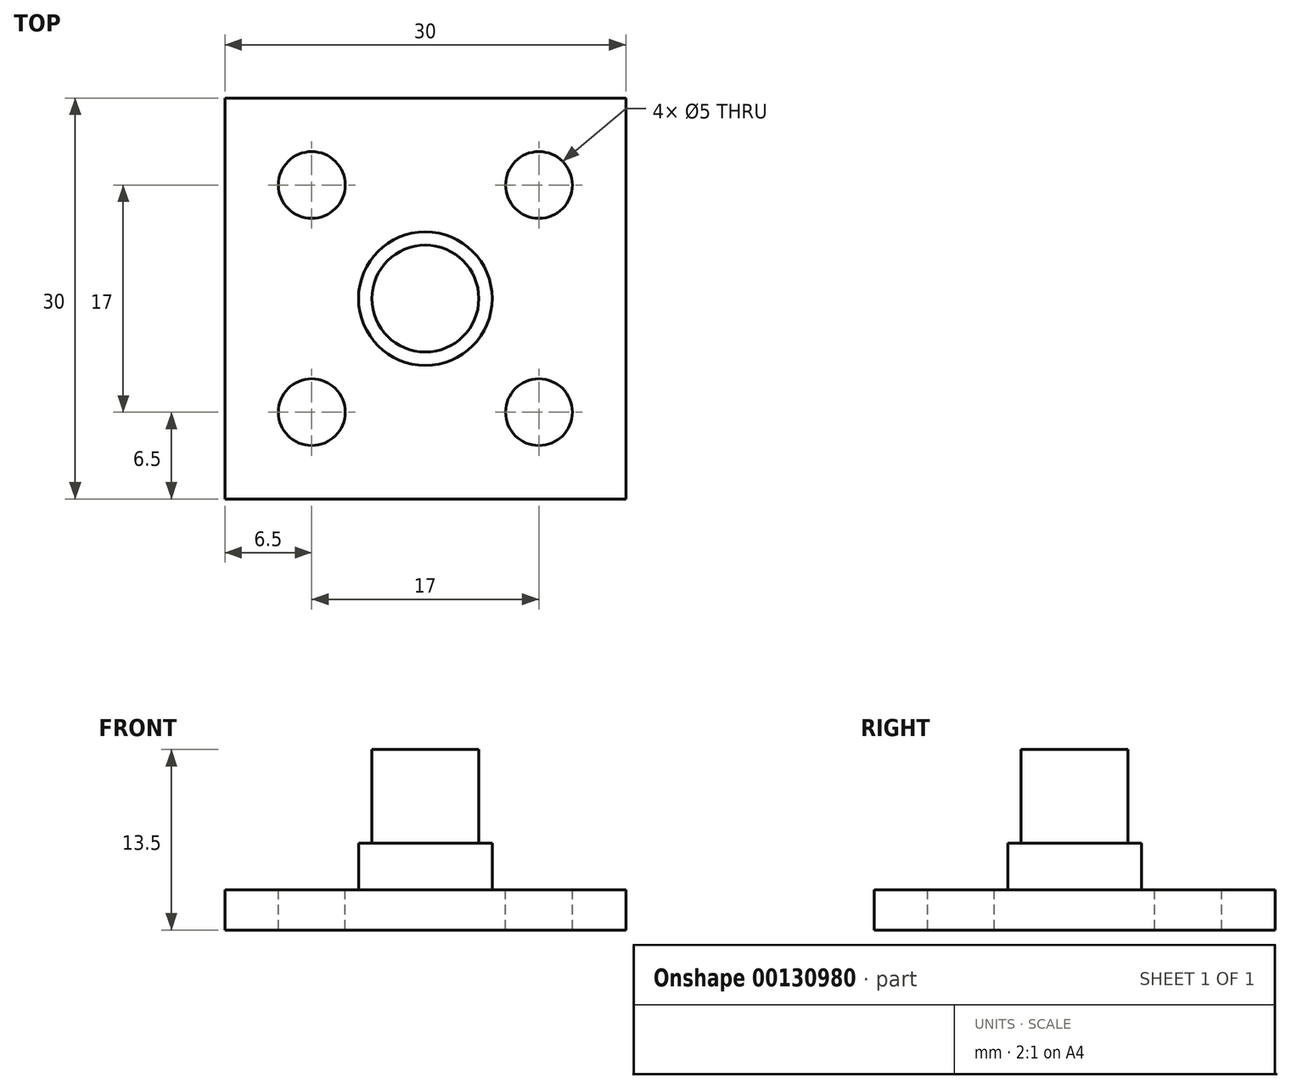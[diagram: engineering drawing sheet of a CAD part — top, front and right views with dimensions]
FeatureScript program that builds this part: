
annotation { "Feature Type Name" : "Feature", "Feature Type Description" : "" }
export const myFeature = defineFeature(function(context is Context, id is Id, definition is map)
    precondition{}
    {
        {
            var Q0;
            Q0=qCreatedBy(makeId("Top.planeOp"),FACE);
            var sketch = newSketch(context, id + "F0", { "sketchPlane" : qUnion([Q0])});
            skLineSegment(sketch, "E0.bottom", {"start": v(15, 15) * mm, "end": v(-15, 15) * mm});
            skLineSegment(sketch, "E0.top", {"start": v(15, -15) * mm, "end": v(-15, -15) * mm});
            skLineSegment(sketch, "E0.left", {"start": v(15, 15) * mm, "end": v(15, -15) * mm});
            skLineSegment(sketch, "E0.right", {"start": v(-15, 15) * mm, "end": v(-15, -15) * mm});
            skPoint(sketch, "E0.middle", {"position": v(0, 0) * mm});
            skCircle(sketch, "E1", {"center": v(0, 0) * mm, "radius": 4 * mm});
            skCircle(sketch, "E2.0", {"center": v(0, 0) * mm, "radius": 5 * mm});
            skSolve(sketch);
        }
        {
            var Q0;
            Q0=makeQuery(id+"F0.imprint","IMPRINT",FACE,{"disambiguationData":[TD([[makeQuery(id+"F0.imprint","IMPRINT",EDGE,{"derivedFrom":sQuery(id+"F0.wireOp",EDGE,"E0.bottom")}),1.0]])]});
            extrude(context, id + "F1", {"entities" : qUnion([Q0]), "depth" : 3 * mm});
        }
        {
            var Q0;
            Q0=makeQuery(id+"F0.imprint","IMPRINT",FACE,{"disambiguationData":[TD([[makeQuery(id+"F0.imprint","IMPRINT",EDGE,{"derivedFrom":sQuery(id+"F0.wireOp",EDGE,"E1")}),-1.0]])]});
            extrude(context, id + "F2", {"entities" : qUnion([Q0]), "operationType" : NewBodyOperationType.ADD, "depth" : 6.5 * mm});
        }
        {
            var Q0;
            Q0=makeQuery(id+"F0.imprint","IMPRINT",FACE,{"disambiguationData":[TD([[makeQuery(id+"F0.imprint","IMPRINT",EDGE,{"derivedFrom":sQuery(id+"F0.wireOp",EDGE,"E1")}),1.0]])]});
            extrude(context, id + "F3", {"entities" : qUnion([Q0]), "operationType" : NewBodyOperationType.ADD, "depth" : 13.5 * mm});
        }
        {
            var Q0;
            Q0=makeQuery(id+"F1.opExtrude","CAP_FACE",FACE,{"disambiguationData":[OSD([sQuery(id+"F0.wireOp",EDGE,"E0.bottom"),sQuery(id+"F0.wireOp",EDGE,"E0.top"),sQuery(id+"F0.wireOp",EDGE,"E0.left"),sQuery(id+"F0.wireOp",EDGE,"E0.right"),sQuery(id+"F0.wireOp",EDGE,"E2.0")])],"isStart":false});
            var sketch = newSketch(context, id + "F4", { "sketchPlane" : qUnion([Q0])});
            skPoint(sketch, "E3", {"position": v(8.5, 8.5) * mm});
            skPoint(sketch, "E4.1.0", {"position": v(-8.5, 8.5) * mm});
            skPoint(sketch, "E4.2.0", {"position": v(-8.5, -8.5) * mm});
            skPoint(sketch, "E4.3.0", {"position": v(8.5, -8.5) * mm});
            skPoint(sketch, "E4.center", {"position": v(0, 0) * mm});
            skSolve(sketch);
        }
        {
            var Q0;
            Q0=sQuery(id+"F4.wireOp",VERTEX,"E3");
            var Q1;
            Q1=sQuery(id+"F4.wireOp",VERTEX,"E4.1.0");
            var Q2;
            Q2=sQuery(id+"F4.wireOp",VERTEX,"E4.2.0");
            var Q3;
            Q3=sQuery(id+"F4.wireOp",VERTEX,"E4.3.0");
            var Q4;
            Q4=makeQuery(id+"F1.opExtrude","SWEPT_BODY",BODY,{"disambiguationData":[OSD([sQuery(id+"F0.wireOp",EDGE,"E0.bottom"),sQuery(id+"F0.wireOp",EDGE,"E0.top"),sQuery(id+"F0.wireOp",EDGE,"E0.left"),sQuery(id+"F0.wireOp",EDGE,"E0.right"),sQuery(id+"F0.wireOp",EDGE,"E2.0")])]});
            hole(context, id + "F5", {"style" : HoleStyle.SIMPLE, "endStyle" : HoleEndStyle.THROUGH, "holeDiameter" : 5 * mm, "locations" : qUnion([Q0, Q1, Q2, Q3]), "scope" : qUnion([Q4]), "isTappedThrough" : true});
        }
        {
            var Q0;
            Q0=makeQuery(id+"F1.opExtrude","SWEPT_BODY",BODY,{"disambiguationData":[OSD([sQuery(id+"F0.wireOp",EDGE,"E0.bottom"),sQuery(id+"F0.wireOp",EDGE,"E0.top"),sQuery(id+"F0.wireOp",EDGE,"E0.left"),sQuery(id+"F0.wireOp",EDGE,"E0.right"),sQuery(id+"F0.wireOp",EDGE,"E2.0")])]});
            transform(context, id + "F6", {"entities" : qUnion([Q0]), "transformType" : TransformType.TRANSLATION_3D, "dx" : 50 * mm, "dy" : 0 * mm, "dz" : 0 * mm, "makeCopy" : true});
        }
        {
            var Q0;
            Q0=makeQuery(id+"F6.opPattern","COPY",BODY,{"derivedFrom":makeQuery(id+"F1.opExtrude","SWEPT_BODY",BODY,{"disambiguationData":[OSD([sQuery(id+"F0.wireOp",EDGE,"E0.bottom"),sQuery(id+"F0.wireOp",EDGE,"E0.top"),sQuery(id+"F0.wireOp",EDGE,"E0.left"),sQuery(id+"F0.wireOp",EDGE,"E0.right"),sQuery(id+"F0.wireOp",EDGE,"E2.0")])]}),"instanceName":"1"});
            deleteBodies(context, id + "F7", {"entities" : qUnion([Q0])});
        }
    });
